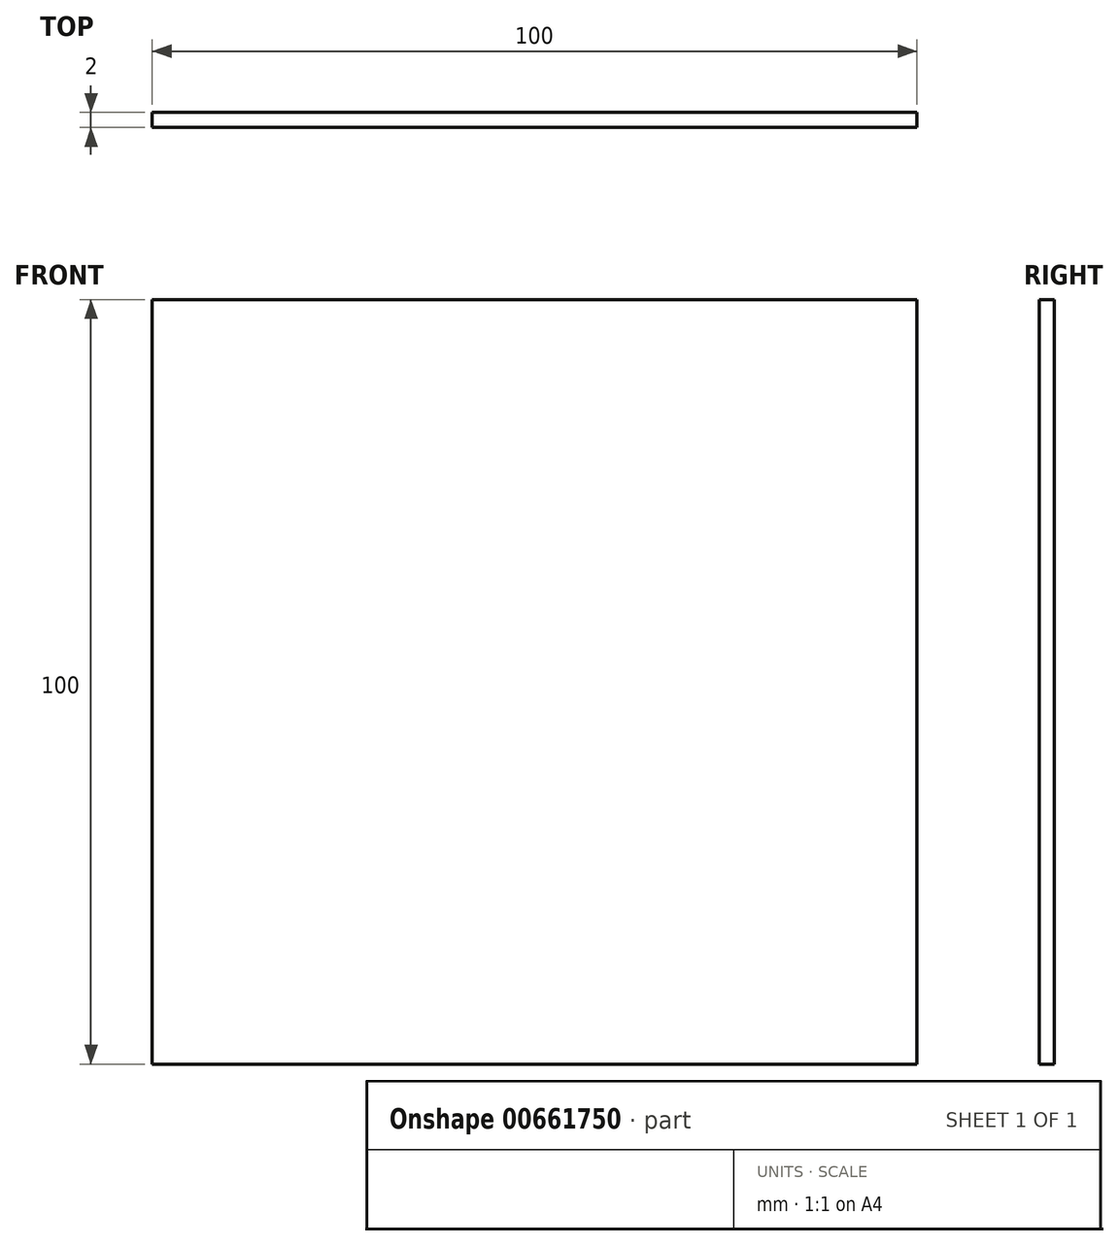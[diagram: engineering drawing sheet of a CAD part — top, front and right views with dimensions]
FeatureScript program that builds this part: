
annotation { "Feature Type Name" : "Feature", "Feature Type Description" : "" }
export const myFeature = defineFeature(function(context is Context, id is Id, definition is map)
    precondition{}
    {
        {
            var Q0;
            Q0=qCreatedBy(makeId("Front.planeOp"),FACE);
            var sketch = newSketch(context, id + "F0", { "sketchPlane" : qUnion([Q0])});
            skLineSegment(sketch, "E0.bottom", {"start": v(50, -50) * mm, "end": v(-50, -50) * mm});
            skLineSegment(sketch, "E0.top", {"start": v(50, 50) * mm, "end": v(-50, 50) * mm});
            skLineSegment(sketch, "E0.left", {"start": v(50, -50) * mm, "end": v(50, 50) * mm});
            skLineSegment(sketch, "E0.right", {"start": v(-50, -50) * mm, "end": v(-50, 50) * mm});
            skPoint(sketch, "E0.middle", {"position": v(0, 0) * mm});
            skSolve(sketch);
        }
        {
            var Q0;
            Q0=makeQuery(id+"F0.imprint","IMPRINT",FACE,{"disambiguationData":[TD([[makeQuery(id+"F0.imprint","IMPRINT",EDGE,{"derivedFrom":sQuery(id+"F0.wireOp",EDGE,"E0.bottom")}),-1.0]])]});
            extrude(context, id + "F1", {"entities" : qUnion([Q0]), "depth" : 2 * mm, "offsetDistance" : 25 * mm});
        }
    });
